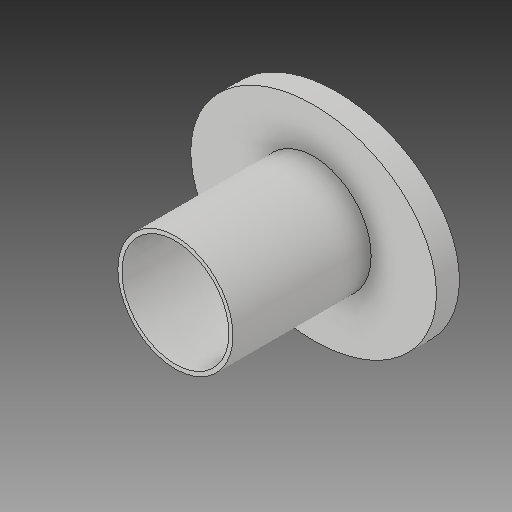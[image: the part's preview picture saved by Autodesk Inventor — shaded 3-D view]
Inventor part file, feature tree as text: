
AUTODESK INVENTOR PART (.ipt)
format: ipt  version: 2018 (Build 220112000, 112)  size: 120,320 bytes
history: native  units: mm
features: sketch x4, other x3
ambient origin geometry x8: Origin, YZ Plane, XZ Plane, XY Plane, X Axis, Y Axis, Z Axis, Center Point
bodies: Solid1 (feature_tree)
feature tree (7):
  other  "Pushfit-adapter-cap.ipt"
  other  "Solid1::Pushfit-adapter-cap.ipt"
  other  "TaggingFeature1"
  sketch  "Sketch1"  dims[d0=10.0mm]
  sketch  "Sketch2"
  sketch  "Sketch3"
  sketch  "Sketch4"
